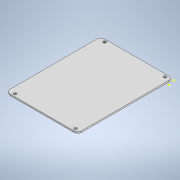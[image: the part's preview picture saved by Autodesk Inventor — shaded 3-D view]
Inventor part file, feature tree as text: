
AUTODESK INVENTOR PART (.ipt)
format: ipt  version: 2022 (Build 260153000, 153)  size: 563,712 bytes
history: native  units: mm
features: extrude x24, sketch x24, projected_geometry x6
ambient origin geometry x8: Origin, YZ Plane, XZ Plane, XY Plane, X Axis, Y Axis, Z Axis, Center Point
bodies: Body1 (feature_tree)
feature tree (54):
  extrude  "Extrusion8"  Depth=3.0mm TaperAngle=0.0deg
  extrude  "Extrusion9"  Depth=67.15mm
  extrude  "Extrusion10"  Depth=8.0mm
  extrude  "Extrusion11"  Depth=8.0mm
  extrude  "Extrusion12"  Depth=11.895mm
  extrude  "Extrusion13"  Depth=9.553mm
  extrude  "Extrusion14"  Depth=8.684mm
  sketch  "Sketch19"  dims[d82=7.81mm d83=8.684mm]
  extrude  "Extrusion16"  Depth=8.602mm
  extrude  "Extrusion17"  Depth=2.5mm
  extrude  "Extrusion18"  Depth=1.0mm
  extrude  "Extrusion19"  Depth=1.5mm
  extrude  "Extrusion20"  Depth=9.0mm TaperAngle=0.0deg
  extrude  "Extrusion21"  Depth=2.0mm
  extrude  "Extrusion24"  Depth=2.0mm
  extrude  "Extrusion25"  Depth=3.0mm TaperAngle=0.0deg
  sketch  "Sketch34"  dims[d117=3.0mm d118=3.0mm]
  extrude  "Extrusion26"  Depth=3.0mm
  extrude  "Extrusion27"  Depth=3.0mm
  extrude  "Extrusion28"  TaperAngle=0.0deg  [1 undecoded]
  extrude  "Extrusion29"  Depth=15.5mm
  extrude  "Extrusion30"  Depth=20.5mm
  extrude  "Extrusion31"  Depth=8.0mm
  extrude  "Extrusion32"  Depth=8.0mm
  extrude  "Extrusion33"  Depth=5.0mm
  extrude  "Extrusion34"  Depth=8.0mm TaperAngle=0.0deg
  sketch  "Sketch12"  dims[d68=3.0mm d69=0.0mm d70=3.0mm d71=0.0mm]
  projected_geometry  "Projected Loop1"
  projected_geometry  "Projected Loop2"
  sketch  "Sketch14"  dims[d72=71.586mm d73=67.15mm]
  sketch  "Sketch15"  dims[d74=8.0mm d75=8.0mm]
  sketch  "Sketch16"  dims[d76=8.0mm d77=8.0mm]
  sketch  "Sketch17"  dims[d78=7.81mm d79=11.895mm]
  sketch  "Sketch18"  dims[d80=8.44mm d81=9.553mm]
  sketch  "Sketch21"  dims[d84=7.81mm d85=8.602mm]
  projected_geometry  "Projected Loop3"
  sketch  "Sketch22"  dims[d86=3.0mm d87=0.0mm d88=2.5mm]
  projected_geometry  "Projected Loop4"
  projected_geometry  "Projected Loop5"
  sketch  "Sketch23"  dims[d89=3.0mm d90=0.0mm d91=1.0mm]
  sketch  "Sketch25"  dims[d92=1.5mm d93=0.0mm d94=5.65mm]
  sketch  "Sketch26"  dims[d95=9.0mm d96=11.17mm d97=0.0mm]
  sketch  "Sketch27"  dims[d98=2.0mm d99=2.0mm]
  sketch  "Sketch32"  dims[d100=2.5mm d101=0.0mm d112=2.0mm]
  sketch  "Sketch33"  dims[d113=2.0mm d114=0.0mm d115=3.0mm d116=0.0mm]
  sketch  "Sketch35"  dims[d119=3.0mm d120=3.0mm]
  sketch  "Sketch37"  dims[d121=0.5mm d122=0.0mm d123=0.0mm]
  sketch  "Sketch38"  dims[d124=0.0mm d125=15.5mm]
  sketch  "Sketch39"  dims[d126=0.0mm d127=20.5mm]
  sketch  "Sketch40"  dims[d128=8.0mm d129=8.0mm]
  projected_geometry  "Projected Loop6"
  sketch  "Sketch41"  dims[d130=8.0mm d131=8.0mm]
  sketch  "Sketch43"  dims[d132=5.3mm d133=5.0mm]
  sketch  "Sketch44"  dims[d134=0.0mm d135=8.0mm d136=0.0mm d137=8.0mm d138=0.0mm d139=3.0mm d140=3.0mm d141=3.0mm d142=3.0mm d143=6.0mm d144=0.0mm d160=100.0mm d161=0.0mm d162=10.0mm d163=0.0mm d164=14.5mm d166=0.74mm d167=100.0mm d168=0.0mm d170=3.0mm d171=3.0mm d172=3.0mm d173=3.0mm d174=5.0mm d175=0.0mm d176=8.0mm d177=8.0mm d178=8.0mm d179=8.0mm d180=75.0mm d181=53.0mm d182=17.3mm d183=2.0mm d184=2.0mm d185=7.6mm d186=2.1mm d187=2.1mm d188=14.7mm d189=13.7mm d190=10.0mm d191=20.0mm d192=3.0mm d193=0.0mm d194=3.0mm d195=3.0mm d196=3.0mm d197=3.0mm d198=5.0mm d199=0.0mm d200=8.0mm d201=8.0mm d202=8.3mm d203=10.0mm d204=10.0mm d205=1.9mm d206=0.0mm d207=10.0mm d208=0.0mm d209=3.0mm d211=3.0mm d212=4.0mm d213=0.0mm d216=22.55489mm d217=8.861037mm d218=2.582mm d219=4.0mm d220=0.0mm d221=8.588357mm d222=5.0mm d223=5.0mm d224=0.0mm d225=10.0mm d226=0.0mm d227=2.85mm d228=14.0mm d229=20.0mm d230=4.0mm d165=0.872665mm]
note: 1 required parameter value undecoded (feature->parameter linkage not recoverable at this tier; creation-order binding heuristic only, values carry confidence <= 0.55)
